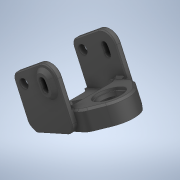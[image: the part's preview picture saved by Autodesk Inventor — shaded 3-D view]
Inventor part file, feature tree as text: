
AUTODESK INVENTOR PART (.ipt)
format: ipt  version: 2020 (Build 240168000, 168)  size: 476,672 bytes
history: native  units: mm
features: extrude x9, sketch x7, projected_geometry x3, chamfer x2, fillet x2
ambient origin geometry x8: Origin, YZ Plane, XZ Plane, XY Plane, X Axis, Y Axis, Z Axis, Center Point
bodies: Volumenkörper1 (feature_tree), Body1 (feature_tree)
feature tree (23):
  extrude  "Extrusion1"  Depth=3.0mm TaperAngle=0.0deg
  extrude  "Extrusion2"  Depth=12.0mm
  chamfer  "Fase1"  [1 undecoded]
  sketch  "Skizze5"  dims[d11=20.0mm]
  extrude  "Extrusion3"  Depth=17.0mm
  extrude  "Extrusion4"  Depth=1.2mm
  sketch  "Skizze6"  dims[d12=6.0mm]
  extrude  "Extrusion5"  Depth=1.2mm TaperAngle=0.0deg
  extrude  "Extrusion6"  Depth=1.2mm TaperAngle=0.0deg
  extrude  "Extrusion8"  Depth=1.2mm TaperAngle=0.0deg
  fillet  "Rundung1"  Radius=2.0mm
  fillet  "Rundung2"  Radius=5.0mm
  chamfer  "Fase2"  Distance=1.0mm Angle=45.0deg
  extrude  "Extrusion9"  Depth=10.8mm
  extrude  "Extrusion10"  Depth=6.0mm
  sketch  "Skizze2"  dims[d0=3.0mm d1=0.0mm d2=3.0mm d3=0.0mm]
  sketch  "Skizze3"  dims[d4=1.7mm d5=2.0mm d6=45.0deg d8=12.0mm]
  projected_geometry  "Projizierte Kontur1"
  projected_geometry  "Projizierte Kontur2"
  sketch  "Skizze7"  dims[d13=13.962634mm d14=0.0mm d15=0.0mm]
  projected_geometry  "Projizierte Kontur3"
  sketch  "Skizze8"  dims[d16=8.34mm d17=0.0mm d18=17.0mm]
  sketch  "Skizze9"  dims[d21=2.5mm d22=8.5mm d23=3.0mm d24=0.0mm d25=11.34mm d26=0.0mm d29=5.34mm d30=0.0mm d31=2.0mm d32=5.0mm d33=1.0mm d34=2.0mm d35=45.0deg d36=10.8mm d37=6.0mm d38=1.0mm d39=10.0mm d40=0.0mm d41=13.5mm d42=1.2mm d43=0.0mm]
note: 1 required parameter value undecoded (feature->parameter linkage not recoverable at this tier; creation-order binding heuristic only, values carry confidence <= 0.55)
